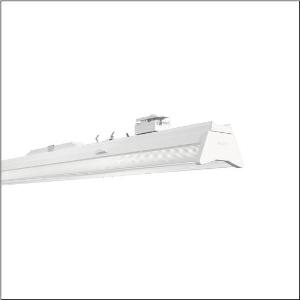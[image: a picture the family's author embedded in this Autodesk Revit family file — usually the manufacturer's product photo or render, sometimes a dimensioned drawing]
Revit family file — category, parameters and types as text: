
# Revit family: licross_21_performance_ho_52td16dn4e5m
name_source: partatom
category: Lighting Fixtures
units: mm (PartAtom-declared; Revit-internal decimal feet)

## family parameters
Cut with Voids When Loaded = No
Host = Face
Light Source = No
Part Type = Normal
Room Calculation Point = No
Round Connector Dimension = Use Diameter
Shared = No

## types (1)
- --- (1 x LED, 14870 lm, 84.9 W, 4000K)
    Apparent Load = 85 VA
    CIE Flux Codes = 63 87 95 78 100
    Color Rendering = 80
    Color Temperature = 4000K
    Default Elevation = 1800 mm
    Description = Licross 21 Performance HO, luminaire insert, of sheet steel, galvanised, coil coated, white, length: 1.500mm, width: 120mm, height: 123mm, LED rated luminous flux: 14.870lm, light colour: 840, SDCM (Standard Deviation of Colour Matching)MacAdam ≤ 3 SDCM (initial), control gear: DALI 2, with plug, 5-pole, with phase selection, mains connection: 220..240V, AC, 50/60Hz, rated input power: 85W, internal wiring halogen-free, primary light control with lens, of plastic, primary optical cover: cover, of PMMA, light emission: direct/indirect distribution, primary light characteristic: symmetric, protection rating (complete): IP54, insulation class (complete): insulation class I (protective earthing), certification: CE, ENEC, VDE, UKCA, protection symbol: D if used in an environment with non-conductive dust loads with corresponding accessories, impact resistance: IK06, permissible ambient temperature for indoor applications: -25..+35°C, corresponds to IFS (International Featured Standards) requirements for safety and quality in the food industry, reducing of maximum allowable ambient temperature of 5°C with ceiling mounting, LABS conformity tested according to VDMA 24364:2018-05, The light source and the operating device comply with the requirements of the Ecodesign Regulation (EU) 2019/2020 and are replaceable in accordance with this regulation, packaging unit: 1 piece
    Height = 114 mm
    Lamp = 1 x LED
    Lamp Light Flux = 14870 lm
    Lamp Power = 84.9 W
    Lamp count = 1
    Length = 1500 mm
    Luminous efficacy = 175 lm/W
    Manufacturer = Siteco
    ModVariant = No
    Model = 52TD16DN4E5M
    Mounting Place = Ceiling
    Mounting Type = Pendant
    Number of Poles = 1
    OnlyDefault = Yes
    Power Factor = 1
    Product Name = Licross 21 Performance HO
    Product group = luminaire insert | ceiling pendant
    ProductGroupID = 901
    Protection Class = Protection class I
    Protection Degree = IP 54
    RLX_Detail_Level = 1
    RLX_Emergency_Light_Flux = 0 lm
    RLX_Emergency_Type = 0
    RLX_Emergency_Type_DB = No
    RlxData = <blob elided: 34293 chars, md5=c61cb3fb>
    Socket = socket
    Standby Power = 0 W
    System Light Flux = 14870 lm
    System Power = 85 W
    Type Comments = factory setting: luminous flux: 100 % | dim-lin: 254 | 484 mA
    Type Image = l_1256138.jpg
    URL = http://relux.com
    VarID = @adj_131029
    Voltage = 0 V
    Weight = 0.00 kg
    Width = 120 mm

## geometry (parser evidence)
native form markers: Blend x4, Sweep x12
no freeform markers — native parametric forms only
